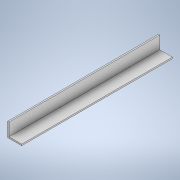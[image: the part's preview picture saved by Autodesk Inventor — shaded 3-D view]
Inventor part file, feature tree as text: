
AUTODESK INVENTOR PART (.ipt)
format: ipt  version: 2021 (Build 250183000, 183)  size: 104,960 bytes
history: native  units: in
note: dims shown in document units (in); Inventor stores cm internally (conversion verified against a paired STEP export)
features: extrude x1, sketch x1
ambient origin geometry x8: Origin, YZ Plane, XZ Plane, XY Plane, X Axis, Y Axis, Z Axis, Center Point
bodies: Solid1 (feature_tree)
feature tree (2):
  extrude  "Extrusion1"  Depth=1.1811in
  sketch  "Sketch1"  dims[d0=1.1811in d1=1.1811in d2=12.5984in d3=0.0in d4=1.063in d5=1.063in]
